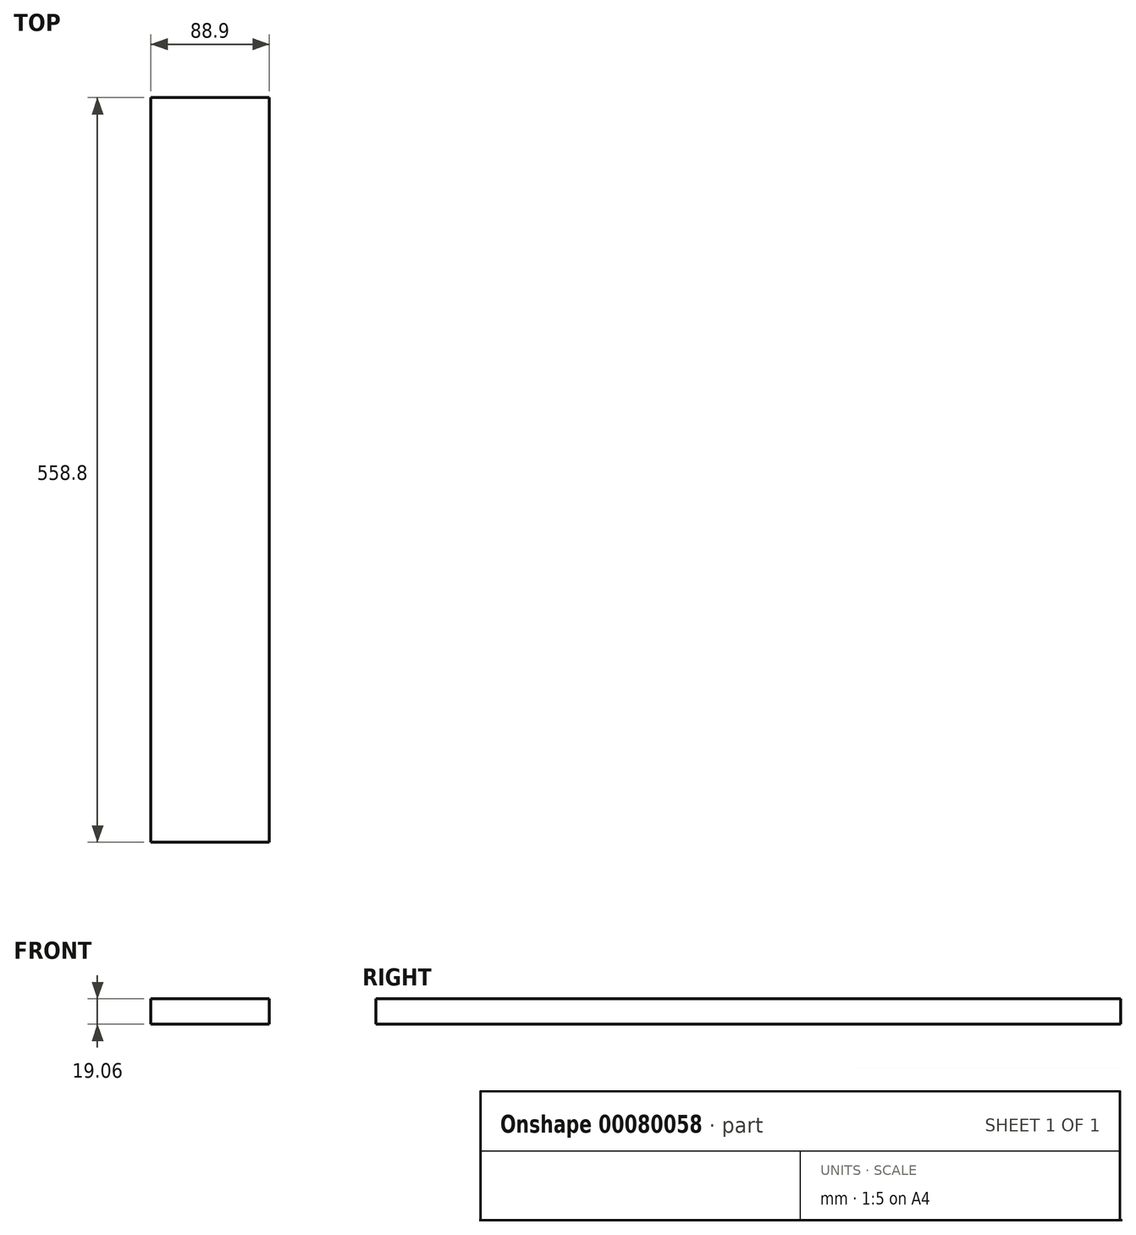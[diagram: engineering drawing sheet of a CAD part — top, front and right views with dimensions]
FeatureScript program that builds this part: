
annotation { "Feature Type Name" : "Feature", "Feature Type Description" : "" }
export const myFeature = defineFeature(function(context is Context, id is Id, definition is map)
    precondition{}
    {
        {
            var Q0;
            Q0=qCreatedBy(makeId("Front.planeOp"),FACE);
            var sketch = newSketch(context, id + "F0", { "sketchPlane" : qUnion([Q0])});
            skLineSegment(sketch, "E0.bottom", {"start": v(-44.45, 9.52) * mm, "end": v(44.45, 9.52) * mm});
            skLineSegment(sketch, "E0.top", {"start": v(-44.45, -9.52) * mm, "end": v(44.45, -9.52) * mm});
            skLineSegment(sketch, "E0.left", {"start": v(-44.45, 9.52) * mm, "end": v(-44.45, -9.52) * mm});
            skLineSegment(sketch, "E0.right", {"start": v(44.45, 9.52) * mm, "end": v(44.45, -9.52) * mm});
            skPoint(sketch, "E0.middle", {"position": v(0, 0) * mm});
            skSolve(sketch);
        }
        {
            var Q0;
            Q0=makeQuery(id+"F0.imprint","IMPRINT",FACE,{"disambiguationData":[TD([[makeQuery(id+"F0.imprint","IMPRINT",EDGE,{"derivedFrom":sQuery(id+"F0.wireOp",EDGE,"E0.bottom")}),-1.0]])]});
            extrude(context, id + "F1", {"entities" : qUnion([Q0]), "endBound" : BoundingType.SYMMETRIC, "depth" : 558.8 * mm});
        }
    });
